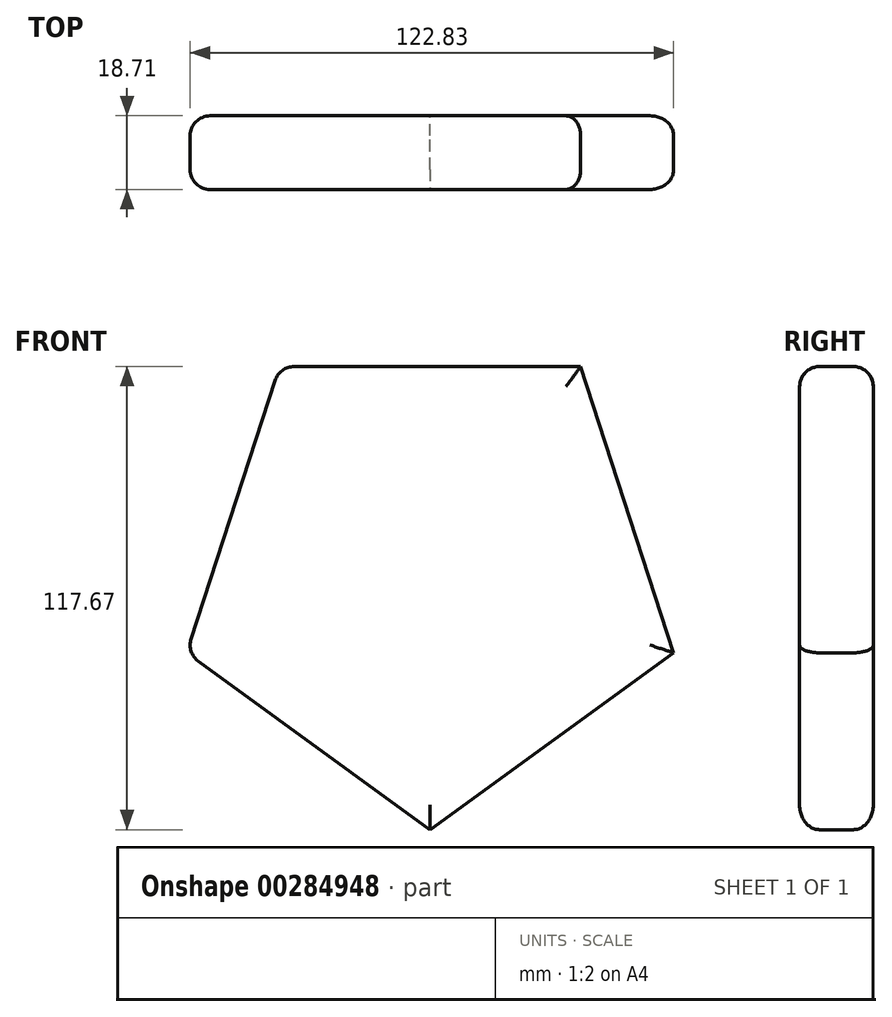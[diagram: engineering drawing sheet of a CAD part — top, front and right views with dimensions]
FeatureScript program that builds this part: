
annotation { "Feature Type Name" : "Feature", "Feature Type Description" : "" }
export const myFeature = defineFeature(function(context is Context, id is Id, definition is map)
    precondition{}
    {
        {
            var Q0;
            Q0=qCreatedBy(makeId("Front.planeOp"),FACE);
            var sketch = newSketch(context, id + "F0", { "sketchPlane" : qUnion([Q0])});
            skCircle(sketch, "E0.cCircle", {"center": v(0, 0) * mm, "radius": 52.62 * mm, "construction": true});
            skLineSegment(sketch, "E0.0", {"start": v(-38.23, 52.62) * mm, "end": v(38.23, 52.62) * mm});
            skLineSegment(sketch, "E0.1", {"start": v(38.23, 52.62) * mm, "end": v(61.86, -20.1) * mm});
            skLineSegment(sketch, "E0.2", {"start": v(61.86, -20.1) * mm, "end": v(0, -65.05) * mm});
            skLineSegment(sketch, "E0.3", {"start": v(0, -65.05) * mm, "end": v(-61.86, -20.1) * mm});
            skLineSegment(sketch, "E0.4", {"start": v(-61.86, -20.1) * mm, "end": v(-38.23, 52.62) * mm});
            skPoint(sketch, "E0.0.midPoint", {"position": v(0, 52.62) * mm});
            skSolve(sketch);
        }
        {
            var Q0;
            Q0=makeQuery(id+"F0.imprint","IMPRINT",FACE,{"disambiguationData":[TD([[makeQuery(id+"F0.imprint","IMPRINT",EDGE,{"derivedFrom":sQuery(id+"F0.wireOp",EDGE,"E0.0")}),-1.0]])]});
            extrude(context, id + "F1", {"entities" : qUnion([Q0]), "depth" : 18.7 * mm});
        }
        {
            var Q0;
            Q0=makeQuery(id+"F1.opExtrude","CAP_EDGE",EDGE,{"disambiguationData":[OSD([sQuery(id+"F0.wireOp",EDGE,"E0.1")])],"isStart":false});
            var Q1;
            Q1=makeQuery(id+"F1.opExtrude","CAP_EDGE",EDGE,{"disambiguationData":[OSD([sQuery(id+"F0.wireOp",EDGE,"E0.1")])],"isStart":true});
            var Q2;
            Q2=makeQuery(id+"F1.opExtrude","CAP_EDGE",EDGE,{"disambiguationData":[OSD([sQuery(id+"F0.wireOp",EDGE,"E0.2")])],"isStart":false});
            var Q3;
            Q3=makeQuery(id+"F1.opExtrude","CAP_EDGE",EDGE,{"disambiguationData":[OSD([sQuery(id+"F0.wireOp",EDGE,"E0.2")])],"isStart":true});
            var Q4;
            Q4=makeQuery(id+"F1.opExtrude","CAP_EDGE",EDGE,{"disambiguationData":[OSD([sQuery(id+"F0.wireOp",EDGE,"E0.3")])],"isStart":true});
            var Q5;
            Q5=makeQuery(id+"F1.opExtrude","CAP_EDGE",EDGE,{"disambiguationData":[OSD([sQuery(id+"F0.wireOp",EDGE,"E0.3")])],"isStart":false});
            var Q6;
            Q6=makeQuery(id+"F1.opExtrude","CAP_FACE",FACE,{"disambiguationData":[OSD([sQuery(id+"F0.wireOp",EDGE,"E0.0"),sQuery(id+"F0.wireOp",EDGE,"E0.1"),sQuery(id+"F0.wireOp",EDGE,"E0.2"),sQuery(id+"F0.wireOp",EDGE,"E0.3"),sQuery(id+"F0.wireOp",EDGE,"E0.4")])],"isStart":true});
            var Q7;
            Q7=makeQuery(id+"F1.opExtrude","CAP_EDGE",EDGE,{"disambiguationData":[OSD([sQuery(id+"F0.wireOp",EDGE,"E0.0")])],"isStart":false});
            var Q8;
            Q8=makeQuery(id+"F1.opExtrude","CAP_EDGE",EDGE,{"disambiguationData":[OSD([sQuery(id+"F0.wireOp",EDGE,"E0.4")])],"isStart":false});
            var Q9;
            Q9=makeQuery(id+"F1.opExtrude","SWEPT_FACE",FACE,{"disambiguationData":[OSD([sQuery(id+"F0.wireOp",EDGE,"E0.4")])]});
            var Q10;
            Q10=makeQuery(id+"F1.opExtrude","CAP_EDGE",EDGE,{"disambiguationData":[OSD([sQuery(id+"F0.wireOp",EDGE,"E0.0")])],"isStart":true});
            var Q11;
            Q11=makeQuery(id+"F1.opExtrude","CAP_EDGE",EDGE,{"disambiguationData":[OSD([sQuery(id+"F0.wireOp",EDGE,"E0.4")])],"isStart":true});
            fillet(context, id + "F2", {"entities" : qUnion([Q0, Q1, Q2, Q3, Q4, Q5, Q6, Q7, Q8, Q9, Q10, Q11]), "radius" : 5.08 * mm, "tangentPropagation" : true, "allowEdgeOverflow" : false});
        }
    });
